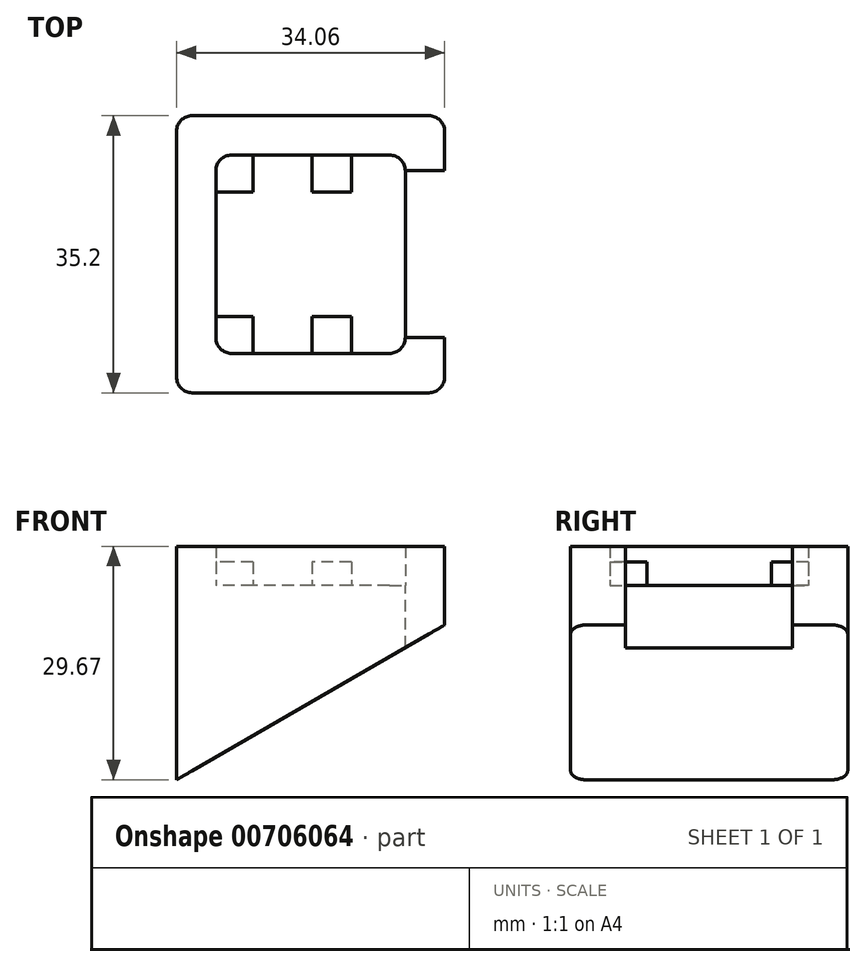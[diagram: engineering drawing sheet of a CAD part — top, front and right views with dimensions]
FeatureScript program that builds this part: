
annotation { "Feature Type Name" : "Feature", "Feature Type Description" : "" }
export const myFeature = defineFeature(function(context is Context, id is Id, definition is map)
    precondition{}
    {
        {
            var Q0;
            Q0=qCreatedBy(makeId("Top.planeOp"),FACE);
            var sketch = newSketch(context, id + "F0", { "sketchPlane" : qUnion([Q0])});
            skLineSegment(sketch, "E0.bottom", {"start": v(10.03, -12.6) * mm, "end": v(-10.03, -12.6) * mm});
            skLineSegment(sketch, "E0.top", {"start": v(10.03, 12.6) * mm, "end": v(-10.03, 12.6) * mm});
            skLineSegment(sketch, "E0.left", {"start": v(12.03, -10.6) * mm, "end": v(12.03, 10.6) * mm});
            skLineSegment(sketch, "E0.right", {"start": v(-12.03, -10.6) * mm, "end": v(-12.03, 10.6) * mm});
            skPoint(sketch, "E0.middle", {"position": v(0, 0) * mm});
            skPoint(sketch, "E1.visualSharp", {"position": v(-12.03, 12.6) * mm});
            skArc(sketch, "E1.filletArc", {"start": v(-10.03, 12.6) * mm, "mid": v(-11.45, 12.01) * mm, "end": v(-12.03, 10.6) * mm});
            skPoint(sketch, "E2.visualSharp", {"position": v(12.03, 12.6) * mm});
            skArc(sketch, "E2.filletArc", {"start": v(12.03, 10.6) * mm, "mid": v(11.45, 12.01) * mm, "end": v(10.03, 12.6) * mm});
            skPoint(sketch, "E3.visualSharp", {"position": v(12.03, -12.6) * mm});
            skArc(sketch, "E3.filletArc", {"start": v(10.03, -12.6) * mm, "mid": v(11.45, -12.01) * mm, "end": v(12.03, -10.6) * mm});
            skPoint(sketch, "E4.visualSharp", {"position": v(-12.03, -12.6) * mm});
            skArc(sketch, "E4.filletArc", {"start": v(-12.03, -10.6) * mm, "mid": v(-11.45, -12.01) * mm, "end": v(-10.03, -12.6) * mm});
            skCircle(sketch, "E5", {"center": v(-10.03, -10.6) * mm, "radius": 1.1 * mm, "construction": true});
            skCircle(sketch, "E6", {"center": v(-10.03, 10.6) * mm, "radius": 1.1 * mm, "construction": true});
            skLineSegment(sketch, "E7", {"start": v(-12.03, 10.6) * mm, "end": v(2.67, 10.6) * mm, "construction": true});
            skCircle(sketch, "E8", {"center": v(2.67, 10.6) * mm, "radius": 1.1 * mm, "construction": true});
            skCircle(sketch, "E9", {"center": v(2.67, -10.6) * mm, "radius": 1.1 * mm, "construction": true});
            skLineSegment(sketch, "E10.bottom", {"start": v(12.03, 10.4) * mm, "end": v(6.33, 10.4) * mm, "construction": true});
            skLineSegment(sketch, "E10.top", {"start": v(12.03, -10.4) * mm, "end": v(6.33, -10.4) * mm, "construction": true});
            skLineSegment(sketch, "E10.left", {"start": v(12.03, 10.4) * mm, "end": v(12.03, -10.4) * mm});
            skLineSegment(sketch, "E10.right", {"start": v(6.33, 10.4) * mm, "end": v(6.33, -10.4) * mm, "construction": true});
            skPoint(sketch, "E11", {"position": v(6.33, 0) * mm});
            skLineSegment(sketch, "E12", {"start": v(-7.33, -12.6) * mm, "end": v(-7.33, -7.9) * mm});
            skLineSegment(sketch, "E13", {"start": v(-7.33, -7.9) * mm, "end": v(-12.03, -7.9) * mm});
            skLineSegment(sketch, "E14", {"start": v(-7.33, 12.6) * mm, "end": v(-7.33, 7.9) * mm});
            skLineSegment(sketch, "E15", {"start": v(-7.33, 7.9) * mm, "end": v(-12.03, 7.9) * mm});
            skLineSegment(sketch, "E16.bottom", {"start": v(5.17, 12.6) * mm, "end": v(0.17, 12.6) * mm});
            skLineSegment(sketch, "E16.top", {"start": v(5.17, 7.9) * mm, "end": v(0.17, 7.9) * mm});
            skLineSegment(sketch, "E16.left", {"start": v(5.17, 12.6) * mm, "end": v(5.17, 7.9) * mm});
            skLineSegment(sketch, "E16.right", {"start": v(0.17, 12.6) * mm, "end": v(0.17, 7.9) * mm});
            skPoint(sketch, "E17", {"position": v(2.67, 7.9) * mm});
            skLineSegment(sketch, "E18.bottom", {"start": v(5.17, -12.6) * mm, "end": v(0.17, -12.6) * mm});
            skLineSegment(sketch, "E18.top", {"start": v(5.17, -7.9) * mm, "end": v(0.17, -7.9) * mm});
            skLineSegment(sketch, "E18.left", {"start": v(5.17, -12.6) * mm, "end": v(5.17, -7.9) * mm});
            skLineSegment(sketch, "E18.right", {"start": v(0.17, -12.6) * mm, "end": v(0.17, -7.9) * mm});
            skLineSegment(sketch, "E19.bottom", {"start": v(-15.03, 17.6) * mm, "end": v(15.03, 17.6) * mm});
            skLineSegment(sketch, "E19.top", {"start": v(-15.03, -17.6) * mm, "end": v(15.03, -17.6) * mm});
            skLineSegment(sketch, "E19.left", {"start": v(-17.03, 15.6) * mm, "end": v(-17.03, -15.6) * mm});
            skLineSegment(sketch, "E19.right", {"start": v(17.03, 15.6) * mm, "end": v(17.03, -15.6) * mm});
            skPoint(sketch, "E20.visualSharp", {"position": v(-17.03, -17.6) * mm});
            skArc(sketch, "E20.filletArc", {"start": v(-17.03, -15.6) * mm, "mid": v(-16.45, -17.01) * mm, "end": v(-15.03, -17.6) * mm});
            skPoint(sketch, "E21.visualSharp", {"position": v(17.03, -17.6) * mm});
            skArc(sketch, "E21.filletArc", {"start": v(15.03, -17.6) * mm, "mid": v(16.45, -17.01) * mm, "end": v(17.03, -15.6) * mm});
            skPoint(sketch, "E22.visualSharp", {"position": v(-17.03, 17.6) * mm});
            skArc(sketch, "E22.filletArc", {"start": v(-15.03, 17.6) * mm, "mid": v(-16.45, 17.01) * mm, "end": v(-17.03, 15.6) * mm});
            skPoint(sketch, "E23.visualSharp", {"position": v(17.03, 17.6) * mm});
            skArc(sketch, "E23.filletArc", {"start": v(17.03, 15.6) * mm, "mid": v(16.45, 17.01) * mm, "end": v(15.03, 17.6) * mm});
            skLineSegment(sketch, "E24", {"start": v(12.03, -10.6) * mm, "end": v(17.03, -10.6) * mm});
            skLineSegment(sketch, "E25", {"start": v(12.03, 10.6) * mm, "end": v(17.03, 10.6) * mm});
            skSolve(sketch);
        }
        {
            var Q0;
            {var subQ8=sQuery(id+"F0.wireOp",EDGE,"E1.filletArc");Q0=makeQuery(id+"F0.imprint","IMPRINT",FACE,{"disambiguationData":[TD([[makeQuery(id+"F0.imprint","IMPRINT",EDGE,{"derivedFrom":subQ8}),-1.0]])]});}
            var Q1;
            {var subQ3=sQuery(id+"F0.wireOp",EDGE,"E2.filletArc");Q1=makeQuery(id+"F0.imprint","IMPRINT",FACE,{"disambiguationData":[TD([[makeQuery(id+"F0.imprint","IMPRINT",EDGE,{"derivedFrom":subQ3}),1.0]])]});}
            var Q2;
            {var subQ1=sQuery(id+"F0.wireOp",EDGE,"E1.filletArc");Q2=makeQuery(id+"F0.imprint","IMPRINT",FACE,{"disambiguationData":[TD([[makeQuery(id+"F0.imprint","IMPRINT",EDGE,{"derivedFrom":subQ1}),1.0]])]});}
            var Q3;
            Q3=makeQuery(id+"F0.imprint","IMPRINT",FACE,{"disambiguationData":[TD([[makeQuery(id+"F0.imprint","IMPRINT",EDGE,{"derivedFrom":sQuery(id+"F0.wireOp",EDGE,"E16.top")}),-1.0]])]});
            var Q4;
            Q4=makeQuery(id+"F0.imprint","IMPRINT",FACE,{"disambiguationData":[TD([[makeQuery(id+"F0.imprint","IMPRINT",EDGE,{"derivedFrom":sQuery(id+"F0.wireOp",EDGE,"E18.top")}),1.0]])]});
            var Q5;
            {var subQ0=sQuery(id+"F0.wireOp",EDGE,"E4.filletArc");Q5=makeQuery(id+"F0.imprint","IMPRINT",FACE,{"disambiguationData":[TD([[makeQuery(id+"F0.imprint","IMPRINT",EDGE,{"derivedFrom":subQ0}),1.0]])]});}
            extrude(context, id + "F1", {"entities" : qUnion([Q0, Q1, Q2, Q3, Q4, Q5]), "oppositeDirection" : true, "depth" : 5 * mm, "offsetDistance" : 25 * mm});
        }
        {
            var Q0;
            {var subQ8=sQuery(id+"F0.wireOp",EDGE,"E1.filletArc");Q0=makeQuery(id+"F0.imprint","IMPRINT",FACE,{"disambiguationData":[TD([[makeQuery(id+"F0.imprint","IMPRINT",EDGE,{"derivedFrom":subQ8}),-1.0]])]});}
            var Q1;
            {var subQ1=sQuery(id+"F0.wireOp",EDGE,"E1.filletArc");Q1=makeQuery(id+"F0.imprint","IMPRINT",FACE,{"disambiguationData":[TD([[makeQuery(id+"F0.imprint","IMPRINT",EDGE,{"derivedFrom":subQ1}),1.0]])]});}
            var Q2;
            Q2=makeQuery(id+"F0.imprint","IMPRINT",FACE,{"disambiguationData":[TD([[makeQuery(id+"F0.imprint","IMPRINT",EDGE,{"derivedFrom":sQuery(id+"F0.wireOp",EDGE,"E16.top")}),-1.0]])]});
            var Q3;
            Q3=makeQuery(id+"F0.imprint","IMPRINT",FACE,{"disambiguationData":[TD([[makeQuery(id+"F0.imprint","IMPRINT",EDGE,{"derivedFrom":sQuery(id+"F0.wireOp",EDGE,"E18.top")}),1.0]])]});
            var Q4;
            {var subQ0=sQuery(id+"F0.wireOp",EDGE,"E4.filletArc");Q4=makeQuery(id+"F0.imprint","IMPRINT",FACE,{"disambiguationData":[TD([[makeQuery(id+"F0.imprint","IMPRINT",EDGE,{"derivedFrom":subQ0}),1.0]])]});}
            extrude(context, id + "F2", {"entities" : qUnion([Q0, Q1, Q2, Q3, Q4]), "operationType" : NewBodyOperationType.ADD, "depth" : 3 * mm, "offsetDistance" : 25 * mm});
        }
        {
            var Q0;
            Q0=makeQuery(id+"F2.opExtrude","CAP_FACE",FACE,{"disambiguationData":[OSD([sQuery(id+"F0.wireOp",EDGE,"E0.bottom"),sQuery(id+"F0.wireOp",EDGE,"E0.top"),sQuery(id+"F0.wireOp",EDGE,"E0.right"),sQuery(id+"F0.wireOp",EDGE,"E2.filletArc"),sQuery(id+"F0.wireOp",EDGE,"E3.filletArc"),sQuery(id+"F0.wireOp",EDGE,"E12"),sQuery(id+"F0.wireOp",EDGE,"E13"),sQuery(id+"F0.wireOp",EDGE,"E14"),sQuery(id+"F0.wireOp",EDGE,"E15"),sQuery(id+"F0.wireOp",EDGE,"E16.top"),sQuery(id+"F0.wireOp",EDGE,"E16.left"),sQuery(id+"F0.wireOp",EDGE,"E16.right"),sQuery(id+"F0.wireOp",EDGE,"E18.top"),sQuery(id+"F0.wireOp",EDGE,"E18.left"),sQuery(id+"F0.wireOp",EDGE,"E18.right"),sQuery(id+"F0.wireOp",EDGE,"E19.bottom"),sQuery(id+"F0.wireOp",EDGE,"E19.top"),sQuery(id+"F0.wireOp",EDGE,"E19.left"),sQuery(id+"F0.wireOp",EDGE,"E19.right"),sQuery(id+"F0.wireOp",EDGE,"E20.filletArc"),sQuery(id+"F0.wireOp",EDGE,"E21.filletArc"),sQuery(id+"F0.wireOp",EDGE,"E22.filletArc"),sQuery(id+"F0.wireOp",EDGE,"E23.filletArc"),sQuery(id+"F0.wireOp",EDGE,"E24"),sQuery(id+"F0.wireOp",EDGE,"E25")])],"isStart":false});
            var sketch = newSketch(context, id + "F3", { "sketchPlane" : qUnion([Q0])});
            skLineSegment(sketch, "E26.bottom", {"start": v(-10.03, 12.6) * mm, "end": v(10.03, 12.6) * mm});
            skLineSegment(sketch, "E26.top", {"start": v(-10.03, -12.6) * mm, "end": v(10.03, -12.6) * mm});
            skLineSegment(sketch, "E26.left", {"start": v(-12.03, 10.6) * mm, "end": v(-12.03, -10.6) * mm});
            skLineSegment(sketch, "E26.right", {"start": v(12.03, 10.6) * mm, "end": v(12.03, -10.6) * mm});
            skPoint(sketch, "E26.middle", {"position": v(0, 0) * mm});
            skPoint(sketch, "E27.visualSharp", {"position": v(-12.03, -12.6) * mm});
            skArc(sketch, "E27.filletArc", {"start": v(-12.03, -10.6) * mm, "mid": v(-11.45, -12.01) * mm, "end": v(-10.03, -12.6) * mm});
            skPoint(sketch, "E28.visualSharp", {"position": v(-12.03, 12.6) * mm});
            skArc(sketch, "E28.filletArc", {"start": v(-10.03, 12.6) * mm, "mid": v(-11.45, 12.01) * mm, "end": v(-12.03, 10.6) * mm});
            skPoint(sketch, "E29.visualSharp", {"position": v(12.03, 12.6) * mm});
            skArc(sketch, "E29.filletArc", {"start": v(12.03, 10.6) * mm, "mid": v(11.45, 12.01) * mm, "end": v(10.03, 12.6) * mm});
            skPoint(sketch, "E30.visualSharp", {"position": v(12.03, -12.6) * mm});
            skArc(sketch, "E30.filletArc", {"start": v(10.03, -12.6) * mm, "mid": v(11.45, -12.01) * mm, "end": v(12.03, -10.6) * mm});
            skSolve(sketch);
        }
        {
            var Q0;
            {var subQ3=sQuery(id+"F3.wireOp",EDGE,"E27.filletArc");Q0=makeQuery(id+"F3.imprint","IMPRINT",FACE,{"disambiguationData":[TD([[makeQuery(id+"F3.imprint","IMPRINT",EDGE,{"derivedFrom":subQ3}),-1.0]])]});}
            extrude(context, id + "F4", {"entities" : qUnion([Q0]), "operationType" : NewBodyOperationType.ADD, "depth" : 2 * mm, "offsetDistance" : 25 * mm});
        }
        {
            var Q0;
            {var subQ0=sQuery(id+"F0.wireOp",EDGE,"E19.bottom");Q0=makeQuery(id+"F4.boolean.opBoolean","MERGE",FACE,{"derivedFrom":[makeQuery(id+"F2.boolean.opBoolean","MERGE",FACE,{"derivedFrom":[makeQuery(id+"F1.opExtrude","SWEPT_FACE",FACE,{"disambiguationData":[OSD([subQ0])]}),makeQuery(id+"F2.opExtrude","SWEPT_FACE",FACE,{"disambiguationData":[OSD([subQ0])]})]}),makeQuery(id+"F4.opExtrude","SWEPT_FACE",FACE,{"disambiguationData":[OSD([subQ0])]})]});}
            var sketch = newSketch(context, id + "F5", { "sketchPlane" : qUnion([Q0])});
            skLineSegment(sketch, "E31", {"start": v(-15.03, -5) * mm, "end": v(-17.03, -5) * mm, "construction": true});
            skLineSegment(sketch, "E32", {"start": v(17.03, 0) * mm, "end": v(17.03, -33.13) * mm, "construction": true});
            skLineSegment(sketch, "E33", {"start": v(17.03, -5) * mm, "end": v(17.03, -24.67) * mm});
            skLineSegment(sketch, "E34", {"start": v(17.03, -24.67) * mm, "end": v(-17.03, -5) * mm});
            skLineSegment(sketch, "E35", {"start": v(17.03, -5) * mm, "end": v(-17.03, -5) * mm});
            skSolve(sketch);
        }
        {
            var Q0;
            {var subQ6=sQuery(id+"F5.wireOp",EDGE,"E33");Q0=makeQuery(id+"F5.imprint","IMPRINT",FACE,{"disambiguationData":[TD([[makeQuery(id+"F5.imprint","IMPRINT",EDGE,{"derivedFrom":subQ6}),-1.0]])]});}
            var Q1;
            Q1=makeQuery(id+"F1.opExtrude","CAP_VERTEX",VERTEX,{"disambiguationData":[OSD([sQuery(id+"F0.wireOp",EDGE,"E19.top"),sQuery(id+"F0.wireOp",EDGE,"E21.filletArc")])],"isStart":false});
            extrude(context, id + "F6", {"entities" : qUnion([Q0]), "operationType" : NewBodyOperationType.ADD, "endBound" : BoundingType.UP_TO_VERTEX, "oppositeDirection" : true, "depth" : 25 * mm, "endBoundEntityVertex" : qUnion([Q1]), "offsetDistance" : 25 * mm});
        }
        {
            var Q0;
            {var subQ1=sQuery(id+"F0.wireOp",EDGE,"E20.filletArc");var subQ4=sQuery(id+"F5.wireOp",EDGE,"E35");Q0=makeQuery(id+"F6.boolean.opBoolean","SPLIT",FACE,{"disambiguationData":[TD([makeQuery(id+"F1.opExtrude","SWEPT_FACE",FACE,{"disambiguationData":[OSD([subQ1])]})])],"derivedFrom":makeQuery(id+"F6.opExtrude","SWEPT_FACE",FACE,{"disambiguationData":[OSD([subQ4])]})});}
            var Q1;
            {var subQ1=sQuery(id+"F0.wireOp",EDGE,"E22.filletArc");var subQ4=sQuery(id+"F5.wireOp",EDGE,"E35");Q1=makeQuery(id+"F6.boolean.opBoolean","SPLIT",FACE,{"disambiguationData":[TD([makeQuery(id+"F1.opExtrude","SWEPT_FACE",FACE,{"disambiguationData":[OSD([subQ1])]})])],"derivedFrom":makeQuery(id+"F6.opExtrude","SWEPT_FACE",FACE,{"disambiguationData":[OSD([subQ4])]})});}
            var Q2;
            {var subQ0=sQuery(id+"F5.wireOp",EDGE,"E35");var subQ3=sQuery(id+"F0.wireOp",EDGE,"E23.filletArc");Q2=makeQuery(id+"F6.boolean.opBoolean","SPLIT",FACE,{"disambiguationData":[TD([makeQuery(id+"F1.opExtrude","SWEPT_FACE",FACE,{"disambiguationData":[OSD([subQ3])]})])],"derivedFrom":makeQuery(id+"F6.opExtrude","SWEPT_FACE",FACE,{"disambiguationData":[OSD([subQ0])]})});}
            var Q3;
            {var subQ0=sQuery(id+"F0.wireOp",EDGE,"E21.filletArc");var subQ4=sQuery(id+"F5.wireOp",EDGE,"E35");Q3=makeQuery(id+"F6.boolean.opBoolean","SPLIT",FACE,{"disambiguationData":[TD([makeQuery(id+"F1.opExtrude","SWEPT_FACE",FACE,{"disambiguationData":[OSD([subQ0])]})])],"derivedFrom":makeQuery(id+"F6.opExtrude","SWEPT_FACE",FACE,{"disambiguationData":[OSD([subQ4])]})});}
            extrude(context, id + "F7", {"entities" : qUnion([Q0, Q1, Q2, Q3]), "operationType" : NewBodyOperationType.REMOVE, "oppositeDirection" : true, "depth" : 25 * mm, "offsetDistance" : 25 * mm});
        }
        {
            var Q0;
            Q0=makeQuery(id+"F6.boolean.opBoolean","SPLIT",FACE,{"disambiguationData":[TD([makeQuery(id+"F1.opExtrude","SWEPT_FACE",FACE,{"disambiguationData":[OSD([sQuery(id+"F0.wireOp",EDGE,"E0.left")])]})])],"derivedFrom":makeQuery(id+"F6.opExtrude","SWEPT_FACE",FACE,{"disambiguationData":[OSD([sQuery(id+"F5.wireOp",EDGE,"E35")])]})});
            extrude(context, id + "F8", {"entities" : qUnion([Q0]), "operationType" : NewBodyOperationType.REMOVE, "oppositeDirection" : true, "depth" : 25 * mm, "offsetDistance" : 25 * mm});
        }
    });
